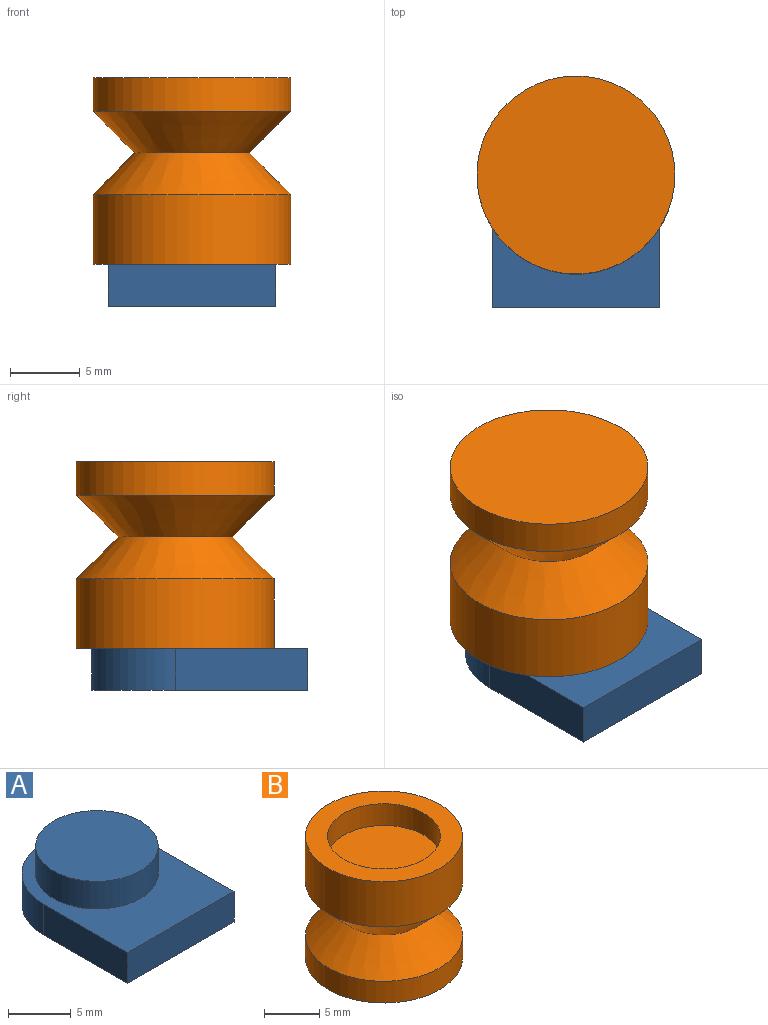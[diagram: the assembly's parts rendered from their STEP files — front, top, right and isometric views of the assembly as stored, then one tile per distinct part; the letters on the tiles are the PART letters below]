
ASSEMBLY  parts=2 mates=1
PART A: 8 faces, bbox 12x15.5x5.7 mm
  f0: cylinder r=4.9mm len=9.8mm, axis (0,0,-1), area 83.1mm2, adj f1,f7
  f1: plane 9.8x9.8mm, normal (0,0,1), area 75.4mm2, adj f0
  f2: plane 9.5x3mm, normal (1,0,0), area 28.5mm2, adj f3,f5,f6,f7
  f3: cylinder r=6mm len=12mm, axis (0,0,1), area 56.5mm2, adj f2,f4,f6,f7
  f4: plane 9.5x3mm, normal (-1,0,0), area 28.5mm2, adj f3,f5,f6,f7
  f5: plane 12x3mm, normal (0,-1,0), area 36mm2, adj f2,f4,f6,f7
  f6: plane 15.5x12mm, normal (0,0,-1), area 170.5mm2, adj f2,f3,f4,f5
  f7: plane 15.5x12mm, normal (0,0,1), area 95.1mm2, adj f0,f2,f3,f4,f5
PART B: 8 faces, bbox 14.2x14.2x13.4 mm
  f0: plane 14.2x14.2mm, normal (0,0,-1), area 158.4mm2, adj f1
  f1: cylinder r=7.1mm len=14.2mm, axis (0,0,1), area 107.1mm2, adj f0,f2
  f2: cone r=7.1mm half-angle=45deg, axis (0,0,-1), area 149.3mm2, adj f1,f3
  f3: cone r=4.1mm half-angle=45deg, axis (0,0,1), area 149.3mm2, adj f2,f4
  f4: cylinder r=7.1mm len=14.2mm, axis (0,0,1), area 223.1mm2, adj f3,f5
  f5: plane 14.2x14.2mm, normal (0,0,1), area 76.7mm2, adj f4,f6
  f6: cylinder r=5.1mm len=10.2mm, axis (0,0,1), area 76.9mm2, adj f5,f7
  f7: plane 10.2x10.2mm, normal (0,0,1), area 81.7mm2, adj f6
PLACE A at identity
PLACE B rot(axis=(1,0,0),180deg) t=(0,0,13.4)mm
MATE fastened B.f1 <-> A.f0  axis (0,0,-1) through (0,0,0)mm
